# Revit family: CAMERA OUTDOOR
name_source: partatom
category: Security Devices
units: mm (PartAtom-declared; Revit-internal decimal feet)

## family parameters
Always vertical = No
Cut with Voids When Loaded = No
Maintain Annotation Orientation = No
OmniClass Number = 23.85.30.17.14
OmniClass Title = Video Surveillance
Part Type = Normal
Room Calculation Point = No
Round Connector Dimension = Use Diameter
Shared = No
Work Plane-Based = No

## types (1)
- CCTV_Outdoor
    FOV Focal Length Maximum = 100
    FOV Focal Length Minimum = 1
    FOV Horizontal Maximum = 89.00°
    FOV Horizontal Minimum = 33.00°
    FOV Horizontal Resolution = 2560
    FOV Vertical Resolution = 1920
    Metric = Yes
    Origin Horizontal = 400 mm  [stored 1.31234 ft]
    Origin Vertical = -64 mm  [stored -0.209974 ft]
    Suspension Length = 725 mm  [stored 2.37861 ft]
    X = 90 mm  [stored 0.295276 ft]
    Y = 200 mm  [stored 0.656168 ft]

note: [stored X ft] marks values corroborated as IEEE doubles in the binary element streams (Revit-internal decimal feet)

## geometry (parser evidence)
native form markers: Blend x2, Sweep x5
no freeform markers — native parametric forms only
